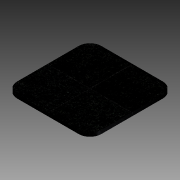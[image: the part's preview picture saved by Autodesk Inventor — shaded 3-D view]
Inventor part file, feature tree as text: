
AUTODESK INVENTOR PART (.ipt)
format: ipt  version: 2013 (Build 170138000, 138)  size: 111,616 bytes
history: native  units: mm
features: extrude x1, fillet x1, sketch x1
ambient origin geometry x8: Origin, YZ Plane, XZ Plane, XY Plane, X Axis, Y Axis, Z Axis, Center Point
bodies: Solid1 (feature_tree)
feature tree (3):
  extrude  "Extrusion1"  Depth=225.0mm
  fillet  "Fillet1"  Radius=225.0mm
  sketch  "Sketch1"  dims[d0=200.0mm d2=225.0mm d3=225.0mm d4=150.0mm d5=37.5mm d6=12.5mm d7=8.1mm d8=9.525mm d9=0.0mm d13=30.0mm]
